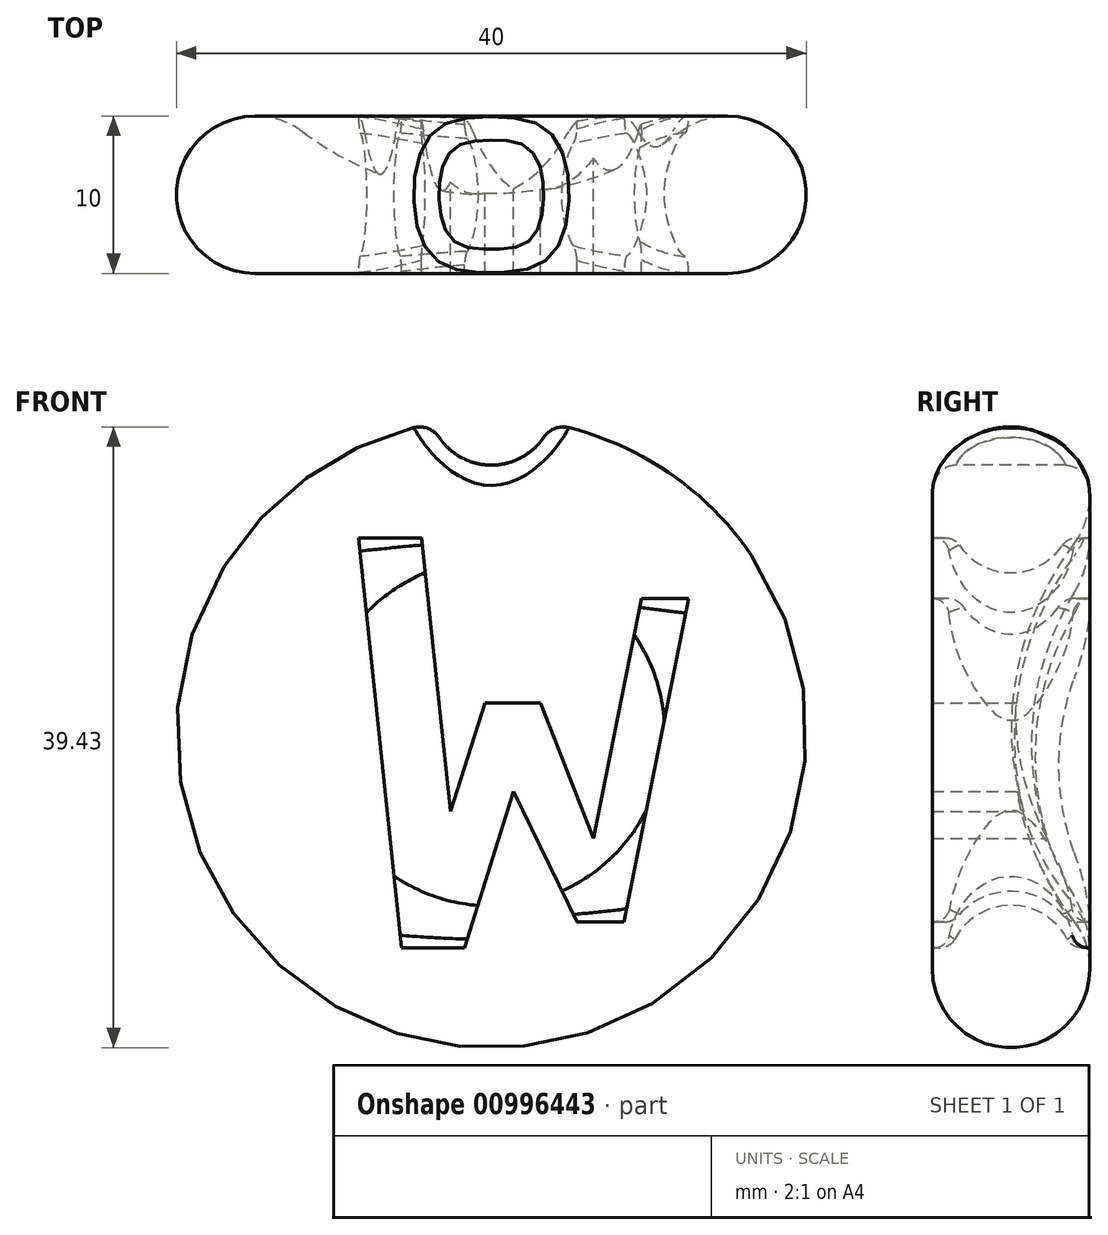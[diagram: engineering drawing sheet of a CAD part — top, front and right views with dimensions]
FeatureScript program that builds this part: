
annotation { "Feature Type Name" : "Feature", "Feature Type Description" : "" }
export const myFeature = defineFeature(function(context is Context, id is Id, definition is map)
    precondition{}
    {
        {
            var Q0;
            Q0=qCreatedBy(makeId("Top.planeOp"),FACE);
            var sketch = newSketch(context, id + "F0", { "sketchPlane" : qUnion([Q0])});
            skArc(sketch, "E0", {"start": v(-12, 9) * mm, "mid": v(-19.74, 6.58) * mm, "end": v(-15, 0) * mm});
            skArc(sketch, "E1", {"start": v(-12, 9) * mm, "mid": v(-6.32, 6.03) * mm, "end": v(0, 5) * mm});
            skLineSegment(sketch, "E2", {"start": v(-15, 0) * mm, "end": v(0, 0) * mm});
            skLineSegment(sketch, "E3", {"start": v(0, 0) * mm, "end": v(0, 5) * mm});
            skSolve(sketch);
        }
        {
            var Q0;
            Q0=makeQuery(id+"F0.imprint","IMPRINT",FACE,{"disambiguationData":[TD([[makeQuery(id+"F0.imprint","IMPRINT",EDGE,{"derivedFrom":sQuery(id+"F0.wireOp",EDGE,"E0")}),1.0]])]});
            var Q1;
            Q1=sQuery(id+"F0.wireOp",EDGE,"E3");
            revolve(context, id + "F1", {"surfaceOperationType" : NewSurfaceOperationType.NEW, "entities" : qUnion([Q0]), "axis" : qUnion([Q1]), "revolveType" : RevolveType.FULL});
        }
        {
            var Q0;
            Q0=qCreatedBy(makeId("Front.planeOp"),FACE);
            cPlane(context, id + "F2", {"entities" : qUnion([Q0]), "cplaneType" : CPlaneType.OFFSET, "offset" : 12 * mm, "oppositeDirection" : true, "width" : 150 * mm, "height" : 150 * mm});
        }
        {
            var Q0;
            Q0=qCreatedBy(id+"F2.planeOp",FACE);
            var sketch = newSketch(context, id + "F3", { "sketchPlane" : qUnion([Q0])});
            skLineSegment(sketch, "E4", {"start": v(12.53, 8.54) * mm, "end": v(9.53, 8.54) * mm});
            skLineSegment(sketch, "E5", {"start": v(9.53, 8.54) * mm, "end": v(6.49, -6.71) * mm});
            skLineSegment(sketch, "E6", {"start": v(6.49, -6.71) * mm, "end": v(3.1, 1.9) * mm});
            skLineSegment(sketch, "E7", {"start": v(3.1, 1.9) * mm, "end": v(-0.4, 1.9) * mm});
            skLineSegment(sketch, "E8", {"start": v(-0.4, 1.9) * mm, "end": v(-2.61, -4.99) * mm});
            skLineSegment(sketch, "E9", {"start": v(-2.61, -4.99) * mm, "end": v(-4.43, 12.39) * mm});
            skLineSegment(sketch, "E10", {"start": v(-4.43, 12.39) * mm, "end": v(-8.43, 12.39) * mm});
            skLineSegment(sketch, "E11", {"start": v(-8.43, 12.39) * mm, "end": v(-5.7, -13.65) * mm});
            skLineSegment(sketch, "E12", {"start": v(-5.7, -13.65) * mm, "end": v(-1.7, -13.65) * mm});
            skLineSegment(sketch, "E13", {"start": v(-1.7, -13.65) * mm, "end": v(1.4, -3.73) * mm});
            skLineSegment(sketch, "E14", {"start": v(1.4, -3.73) * mm, "end": v(5.44, -12) * mm});
            skLineSegment(sketch, "E15", {"start": v(5.44, -12) * mm, "end": v(8.44, -12) * mm});
            skLineSegment(sketch, "E16", {"start": v(8.44, -12) * mm, "end": v(12.53, 8.54) * mm});
            skSolve(sketch);
        }
        {
            var Q0;
            Q0=makeQuery(id+"F3.imprint","IMPRINT",FACE,{"disambiguationData":[TD([[makeQuery(id+"F3.imprint","IMPRINT",EDGE,{"derivedFrom":sQuery(id+"F3.wireOp",EDGE,"E4")}),1.0]])]});
            extrude(context, id + "F4", {"entities" : qUnion([Q0]), "operationType" : NewBodyOperationType.REMOVE, "depth" : 25 * mm, "offsetDistance" : 25 * mm});
        }
        {
            var Q0;
            Q0=qCreatedBy(makeId("Top.planeOp"),FACE);
            var sketch = newSketch(context, id + "F5", { "sketchPlane" : qUnion([Q0])});
            skCircle(sketch, "E17", {"center": v(-15, 5) * mm, "radius": 4 * mm});
            skSolve(sketch);
        }
        {
            var Q0;
            Q0 = qSketchRegion(id + "F5", true);
            var Q1;
            Q1=sQuery(id+"F0.wireOp",EDGE,"E3");
            revolve(context, id + "F6", {"operationType" : NewBodyOperationType.ADD, "surfaceOperationType" : NewSurfaceOperationType.NEW, "entities" : qUnion([Q0]), "axis" : qUnion([Q1]), "revolveType" : RevolveType.FULL});
        }
        {
            var Q0;
            Q0=qCreatedBy(makeId("Front.planeOp"),FACE);
            var sketch = newSketch(context, id + "F7", { "sketchPlane" : qUnion([Q0])});
            skCircle(sketch, "E18", {"center": v(0, 21) * mm, "radius": 4 * mm});
            skSolve(sketch);
        }
        {
            var Q0;
            Q0 = qSketchRegion(id + "F7", true);
            extrude(context, id + "F8", {"entities" : qUnion([Q0]), "operationType" : NewBodyOperationType.REMOVE, "oppositeDirection" : true, "depth" : 25 * mm, "offsetDistance" : 25 * mm});
        }
        {
            var Q0;
            Q0=makeQuery(id+"F8.boolean.opBoolean","INTERSECT",EDGE,{"derivedFrom":[makeQuery(id+"F4.boolean.opBoolean","SPLIT",FACE,{"disambiguationData":[TD([makeQuery(id+"F1.opRevolve","SWEPT_FACE",FACE,{"disambiguationData":[OSD([sQuery(id+"F0.wireOp",EDGE,"E2")])]})])],"derivedFrom":makeQuery(id+"F1.opRevolve","SWEPT_FACE",FACE,{"disambiguationData":[OSD([sQuery(id+"F0.wireOp",EDGE,"E0")])]})}),makeQuery(id+"F8.opExtrude","SWEPT_FACE",FACE,{"disambiguationData":[OSD([sQuery(id+"F7.wireOp",EDGE,"E18")])]})]});
            fillet(context, id + "F9", {"entities" : qUnion([Q0]), "radius" : 1.5 * mm, "tangentPropagation" : true, "allowEdgeOverflow" : false});
        }
        {
            var Q0;
            Q0=makeQuery(id+"F6.boolean.opBoolean","INTERSECT",EDGE,{"disambiguationData":[OD(1.0)],"derivedFrom":[makeQuery(id+"F4.boolean.opBoolean","COPY",FACE,{"derivedFrom":makeQuery(id+"F4.opExtrude","SWEPT_FACE",FACE,{"disambiguationData":[OSD([sQuery(id+"F3.wireOp",EDGE,"E4")])]})}),makeQuery(id+"F6.opRevolve","SWEPT_FACE",FACE,{"disambiguationData":[OSD([sQuery(id+"F5.wireOp",EDGE,"E17")])]})]});
            var Q1;
            Q1=makeQuery(id+"F6.boolean.opBoolean","INTERSECT",EDGE,{"disambiguationData":[OD(0.0)],"derivedFrom":[makeQuery(id+"F4.boolean.opBoolean","COPY",FACE,{"derivedFrom":makeQuery(id+"F4.opExtrude","SWEPT_FACE",FACE,{"disambiguationData":[OSD([sQuery(id+"F3.wireOp",EDGE,"E10")])]})}),makeQuery(id+"F6.opRevolve","SWEPT_FACE",FACE,{"disambiguationData":[OSD([sQuery(id+"F5.wireOp",EDGE,"E17")])]})]});
            var Q2;
            Q2=makeQuery(id+"F6.boolean.opBoolean","INTERSECT",EDGE,{"disambiguationData":[OD(0.0)],"derivedFrom":[makeQuery(id+"F4.boolean.opBoolean","COPY",FACE,{"derivedFrom":makeQuery(id+"F4.opExtrude","SWEPT_FACE",FACE,{"disambiguationData":[OSD([sQuery(id+"F3.wireOp",EDGE,"E12")])]})}),makeQuery(id+"F6.opRevolve","SWEPT_FACE",FACE,{"disambiguationData":[OSD([sQuery(id+"F5.wireOp",EDGE,"E17")])]})]});
            var Q3;
            Q3=makeQuery(id+"F6.boolean.opBoolean","INTERSECT",EDGE,{"disambiguationData":[OD(0.0)],"derivedFrom":[makeQuery(id+"F4.boolean.opBoolean","COPY",FACE,{"derivedFrom":makeQuery(id+"F4.opExtrude","SWEPT_FACE",FACE,{"disambiguationData":[OSD([sQuery(id+"F3.wireOp",EDGE,"E15")])]})}),makeQuery(id+"F6.opRevolve","SWEPT_FACE",FACE,{"disambiguationData":[OSD([sQuery(id+"F5.wireOp",EDGE,"E17")])]})]});
            var Q4;
            Q4=makeQuery(id+"F6.boolean.opBoolean","INTERSECT",EDGE,{"disambiguationData":[OD(1.0)],"derivedFrom":[makeQuery(id+"F4.boolean.opBoolean","COPY",FACE,{"derivedFrom":makeQuery(id+"F4.opExtrude","SWEPT_FACE",FACE,{"disambiguationData":[OSD([sQuery(id+"F3.wireOp",EDGE,"E10")])]})}),makeQuery(id+"F6.opRevolve","SWEPT_FACE",FACE,{"disambiguationData":[OSD([sQuery(id+"F5.wireOp",EDGE,"E17")])]})]});
            var Q5;
            Q5=makeQuery(id+"F6.boolean.opBoolean","INTERSECT",EDGE,{"disambiguationData":[OD(0.0)],"derivedFrom":[makeQuery(id+"F4.boolean.opBoolean","COPY",FACE,{"derivedFrom":makeQuery(id+"F4.opExtrude","SWEPT_FACE",FACE,{"disambiguationData":[OSD([sQuery(id+"F3.wireOp",EDGE,"E4")])]})}),makeQuery(id+"F6.opRevolve","SWEPT_FACE",FACE,{"disambiguationData":[OSD([sQuery(id+"F5.wireOp",EDGE,"E17")])]})]});
            var Q6;
            Q6=makeQuery(id+"F6.boolean.opBoolean","INTERSECT",EDGE,{"disambiguationData":[OD(1.0)],"derivedFrom":[makeQuery(id+"F4.boolean.opBoolean","COPY",FACE,{"derivedFrom":makeQuery(id+"F4.opExtrude","SWEPT_FACE",FACE,{"disambiguationData":[OSD([sQuery(id+"F3.wireOp",EDGE,"E15")])]})}),makeQuery(id+"F6.opRevolve","SWEPT_FACE",FACE,{"disambiguationData":[OSD([sQuery(id+"F5.wireOp",EDGE,"E17")])]})]});
            var Q7;
            Q7=makeQuery(id+"F6.boolean.opBoolean","INTERSECT",EDGE,{"disambiguationData":[OD(1.0)],"derivedFrom":[makeQuery(id+"F4.boolean.opBoolean","COPY",FACE,{"derivedFrom":makeQuery(id+"F4.opExtrude","SWEPT_FACE",FACE,{"disambiguationData":[OSD([sQuery(id+"F3.wireOp",EDGE,"E12")])]})}),makeQuery(id+"F6.opRevolve","SWEPT_FACE",FACE,{"disambiguationData":[OSD([sQuery(id+"F5.wireOp",EDGE,"E17")])]})]});
            fillet(context, id + "F10", {"entities" : qUnion([Q0, Q1, Q2, Q3, Q4, Q5, Q6, Q7]), "radius" : 1 * mm, "tangentPropagation" : true, "allowEdgeOverflow" : false});
        }
    });
